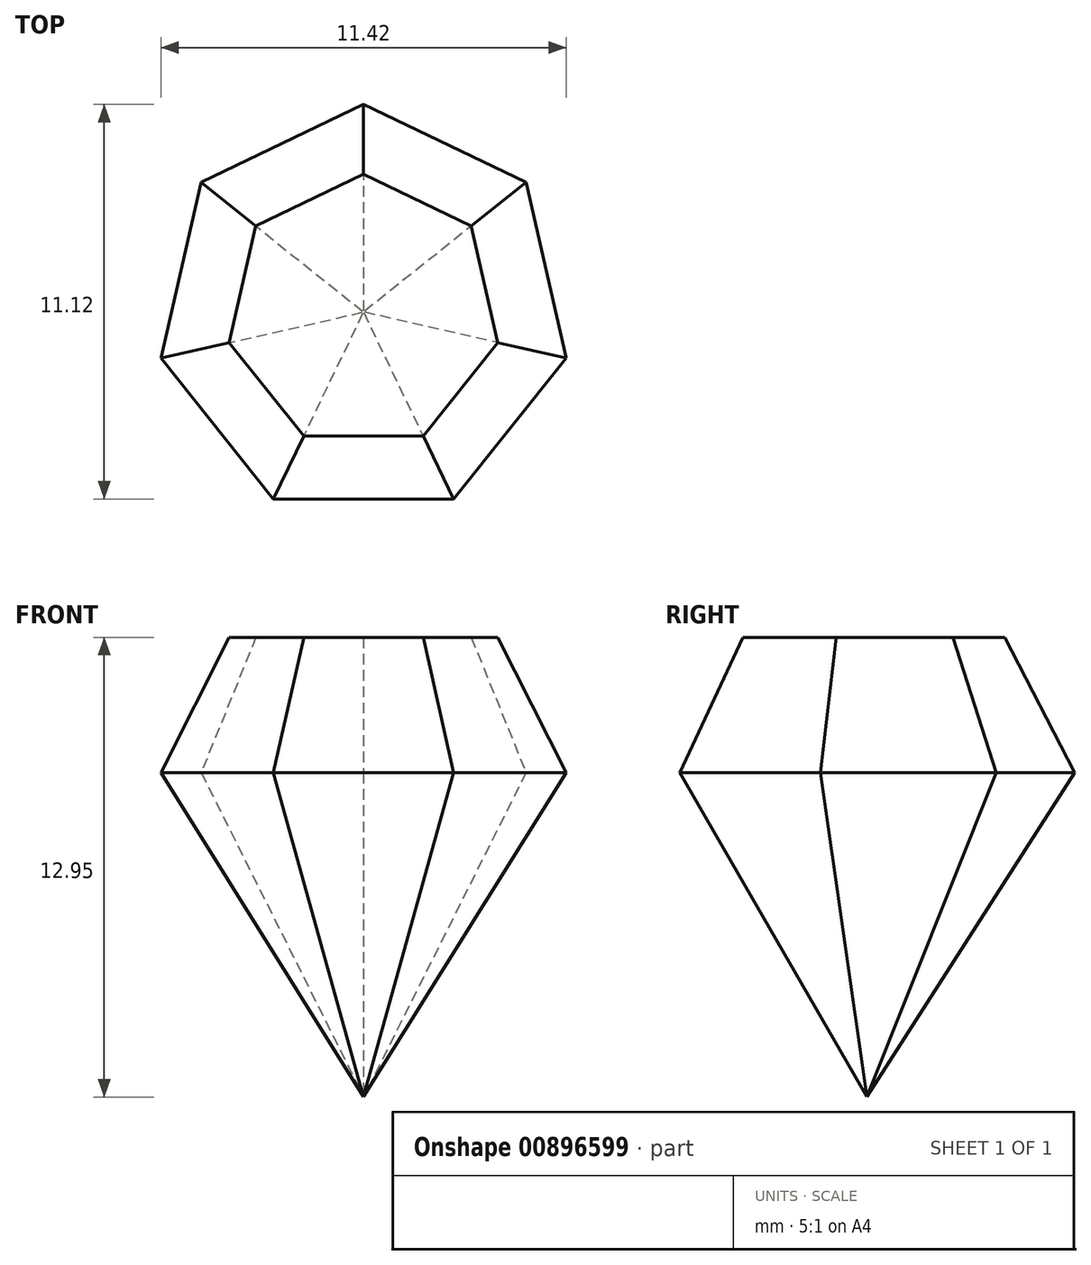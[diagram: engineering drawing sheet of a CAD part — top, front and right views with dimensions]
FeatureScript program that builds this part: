
annotation { "Feature Type Name" : "Feature", "Feature Type Description" : "" }
export const myFeature = defineFeature(function(context is Context, id is Id, definition is map)
    precondition{}
    {
        {
            var Q0;
            Q0=qCreatedBy(makeId("Top.planeOp"),FACE);
            var sketch = newSketch(context, id + "F0", { "sketchPlane" : qUnion([Q0])});
            skCircle(sketch, "E0.cCircle", {"center": v(0, 0) * mm, "radius": 5.27 * mm, "construction": true});
            skLineSegment(sketch, "E0.0", {"start": v(5.7, -1.3) * mm, "end": v(2.54, -5.27) * mm});
            skLineSegment(sketch, "E0.1", {"start": v(2.54, -5.27) * mm, "end": v(-2.54, -5.27) * mm});
            skLineSegment(sketch, "E0.2", {"start": v(-2.54, -5.27) * mm, "end": v(-5.7, -1.3) * mm});
            skLineSegment(sketch, "E0.3", {"start": v(-5.7, -1.3) * mm, "end": v(-4.58, 3.65) * mm});
            skLineSegment(sketch, "E0.4", {"start": v(-4.58, 3.65) * mm, "end": v(0, 5.85) * mm});
            skLineSegment(sketch, "E0.5", {"start": v(0, 5.85) * mm, "end": v(4.58, 3.65) * mm});
            skLineSegment(sketch, "E0.6", {"start": v(4.58, 3.65) * mm, "end": v(5.7, -1.3) * mm});
            skPoint(sketch, "E0.0.midPoint", {"position": v(4.12, -3.29) * mm});
            skSolve(sketch);
        }
        {
            var Q0;
            Q0 = qSketchRegion(id + "F0", true);
            extrude(context, id + "F1", {"entities" : qUnion([Q0]), "depth" : 3.8 * mm, "offsetDistance" : 25.4 * mm, "hasDraft" : true, "draftAngle" : 25 * degree, "draftPullDirection" : true, "hasSecondDirection" : true, "secondDirectionOppositeDirection" : true, "secondDirectionDepth" : 10.16 * mm, "hasSecondDirectionDraft" : true, "secondDirectionDraftAngle" : 30 * degree, "secondDirectionDraftPullDirection" : true});
        }
    });
